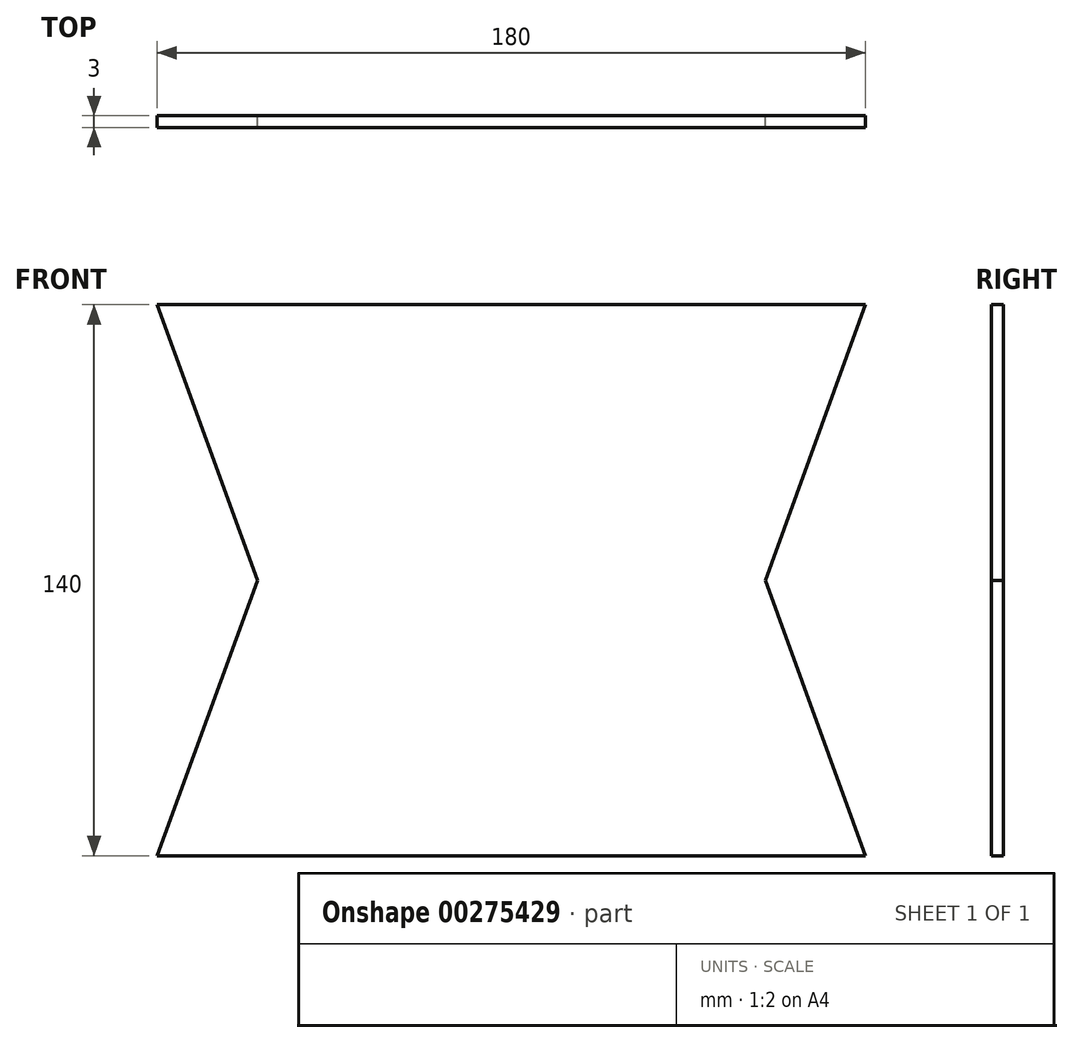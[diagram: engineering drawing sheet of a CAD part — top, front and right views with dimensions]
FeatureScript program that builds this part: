
annotation { "Feature Type Name" : "Feature", "Feature Type Description" : "" }
export const myFeature = defineFeature(function(context is Context, id is Id, definition is map)
    precondition{}
    {
        {
            var Q0;
            Q0=qCreatedBy(makeId("Front.planeOp"),FACE);
            var sketch = newSketch(context, id + "F0", { "sketchPlane" : qUnion([Q0])});
            skLineSegment(sketch, "E0.bottom", {"start": v(-93.08, 36.9) * mm, "end": v(86.92, 36.9) * mm});
            skLineSegment(sketch, "E0.top", {"start": v(-93.08, -103.1) * mm, "end": v(86.92, -103.1) * mm});
            skLineSegment(sketch, "E1", {"start": v(-93.08, 36.9) * mm, "end": v(-67.6, -33.1) * mm});
            skLineSegment(sketch, "E2", {"start": v(-67.6, -33.1) * mm, "end": v(-93.08, -103.1) * mm});
            skLineSegment(sketch, "E3", {"start": v(86.92, 36.9) * mm, "end": v(61.44, -33.1) * mm});
            skLineSegment(sketch, "E4", {"start": v(61.44, -33.1) * mm, "end": v(86.92, -103.1) * mm});
            skPoint(sketch, "E5.center.orphan", {"position": v(-3.08, -33.1) * mm});
            skSolve(sketch);
        }
        {
            var Q0;
            Q0=qSketchRegion(id+"F0",true);
            extrude(context, id + "F1", {"entities" : qUnion([Q0]), "depth" : 3 * mm});
        }
    });
